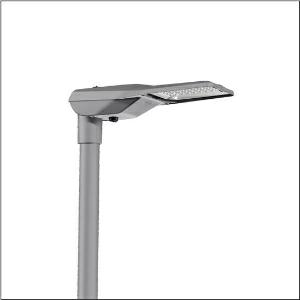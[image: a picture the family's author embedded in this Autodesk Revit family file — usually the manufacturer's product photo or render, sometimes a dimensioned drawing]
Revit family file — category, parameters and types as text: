
# Revit family: streetlight_sl_21_iq_mini___pl52_5xe2h31y08hb_fa04
name_source: partatom
category: Lighting Fixtures
units: mm (PartAtom-declared; Revit-internal decimal feet)

## family parameters
Cut with Voids When Loaded = No
Host = Face
Light Source = No
Part Type = Normal
Room Calculation Point = No
Round Connector Dimension = Use Diameter
Shared = No

## types (1)
- --- (1 x LED, 9580 lm, 71 W, 3000K)
    Apparent Load = 71 VA
    CIE Flux Codes = 27 59 98 100 100
    Color Rendering = 70
    Color Temperature = 3000K
    Default Elevation = 1800 mm
    Description = Streetlight SL 21 iQ mini, mast luminaire, primary light control with lens, of PMMA, primary optical cover: cover, of toughened safety glass, transparent, light distribution: PL52, light emission: direct distribution, primary light characteristic: asymmetric, installation type: post-top, side-entry, LED, High Power LED, rated luminous flux: 9.580lm, luminous efficacy: 135lm/W, light colour: 730, colour temperature: 3000K, control: presetting dimming logarithmic, Street-Remote, Auto-Match, Temp-Guard, Lumen-Switch, Night-Set, Smart-Wire, Light-Fading, Desk-Remote (wireless, voltage-free reading and setting of iQ features in the workshop via application-optimized NFC function/RFID function), optimised constant luminous flux control (CLO 2.0), mains connection: 220..240V, AC, 50/60Hz, start of lifetime: 71W, end of service life: 75W, reduction: 30W, luminaire housing, of diecast aluminium, powder-coated, Siteco® metallic grey (DB 702S), corrosivity category C5 mid according to DIN EN ISO 12944, please order mast flange separately, inclination adjustable: 0°, 5°, 10°, 15°, sealing non-destructively replaceable, multi-level sealing system, length: 628mm, width: 235mm, height: 110mm, mast flange for spigot size: 42mm (side-entry): 5XC10008XM4, 60/48mm (side-entry/post-top): 5XC10108XM2, 76/60mm (side-entry/post-top): 5XC10108XM1, Smart Interface below and above, protection rating (complete): IP66, insulation class (complete): insulation class II (safety insulation), certification: CE, ENEC, ENEC+, VDE, impact resistance: IK09, permissible operating ambient temperature for outdoor applications: -40..+50°C, standard-compliant lighting for roads and squares, packaging unit: 1 piece

Light Distribution: PL52
    Height = 110 mm
    Lamp = 1 x LED
    Lamp Light Flux = 9580 lm
    Lamp Power = 71 W
    Lamp count = 1
    Length = 625 mm
    Luminous efficacy = 135 lm/W
    Manufacturer = Siteco
    ModVariant = No
    Model = 5XE2H31Y08HB
    Number of Poles = 1
    OnlyDefault = Yes
    Power Factor = 1
    Product Name = Streetlight SL 21 iQ mini | PL52
    Product group = mast luminaire | pylon top
    ProductGroupID = 6100
    Protection Class = Protection class II
    Protection Degree = IP 66
    RLX_Detail_Level = 1
    RLX_Emergency_Light_Flux = 0 lm
    RLX_Emergency_Type = 0
    RLX_Emergency_Type_DB = No
    RlxData = <blob elided: 102253 chars, md5=1b755130>
    Socket = socket
    Standby Power = 0 W
    System Light Flux = 9580 lm
    System Power = 71 W
    Type Comments = factory setting: luminous flux: 100 % | dim-lin: 254 | 716 mA
    Type Image = l_1003514.jpg
    URL = http://relux.com
    VarID = @adj_045951
    Voltage = 0 V
    Weight = 0.00 kg
    Width = 234 mm

## geometry (parser evidence)
native form markers: Blend x4, Sweep x10
no freeform markers — native parametric forms only
